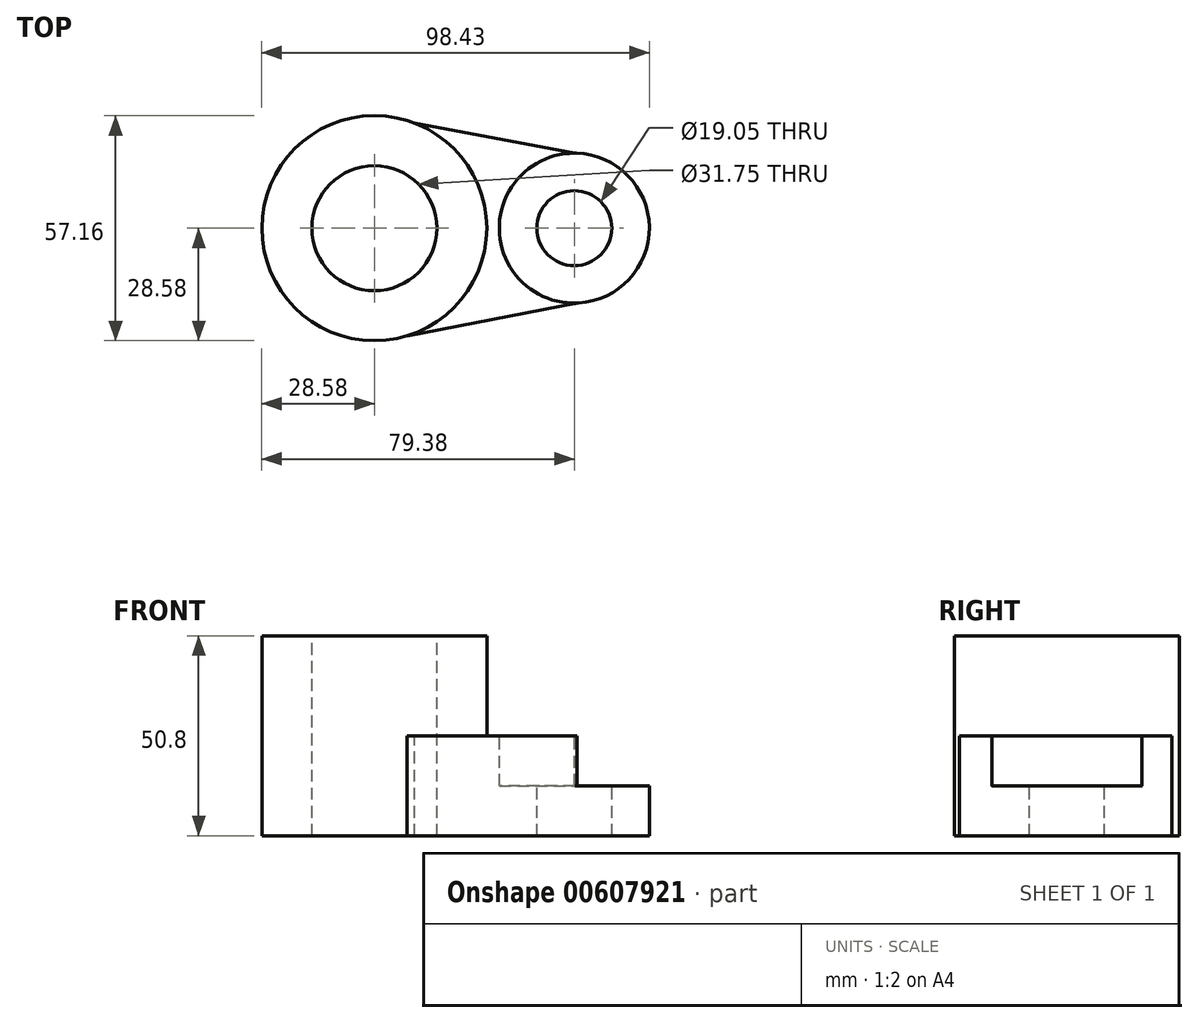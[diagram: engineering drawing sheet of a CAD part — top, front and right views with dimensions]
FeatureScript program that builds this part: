
annotation { "Feature Type Name" : "Feature", "Feature Type Description" : "" }
export const myFeature = defineFeature(function(context is Context, id is Id, definition is map)
    precondition{}
    {
        {
            var Q0;
            Q0=qCreatedBy(makeId("Top.planeOp"),FACE);
            var sketch = newSketch(context, id + "F0", { "sketchPlane" : qUnion([Q0])});
            skCircle(sketch, "E0", {"center": v(0, 0) * mm, "radius": 15.88 * mm});
            skCircle(sketch, "E1", {"center": v(0, 0) * mm, "radius": 28.58 * mm});
            skCircle(sketch, "E2", {"center": v(50.8, 0) * mm, "radius": 19.05 * mm});
            skCircle(sketch, "E3", {"center": v(50.8, 0) * mm, "radius": 9.53 * mm});
            skLineSegment(sketch, "E4", {"start": v(10.28, 26.66) * mm, "end": v(50.88, 19.05) * mm});
            skLineSegment(sketch, "E5", {"start": v(8.3, -27.34) * mm, "end": v(51.47, -19.04) * mm});
            skSolve(sketch);
        }
        {
            var Q0;
            Q0=makeQuery(id+"F0.imprint","IMPRINT",FACE,{"disambiguationData":[TD([[makeQuery(id+"F0.imprint","IMPRINT",EDGE,{"derivedFrom":sQuery(id+"F0.wireOp",EDGE,"E0")}),-1.0]])]});
            var Q1;
            Q1=makeQuery(id+"F0.imprint","IMPRINT",FACE,{"disambiguationData":[TD([[makeQuery(id+"F0.imprint","IMPRINT",EDGE,{"derivedFrom":sQuery(id+"F0.wireOp",EDGE,"E3")}),-1.0]])]});
            var Q2;
            {var subQ0=sQuery(id+"F0.wireOp",EDGE,"E4");Q2=makeQuery(id+"F0.imprint","IMPRINT",FACE,{"disambiguationData":[TD([[makeQuery(id+"F0.imprint","IMPRINT",EDGE,{"derivedFrom":subQ0}),-1.0]])]});}
            extrude(context, id + "F1", {"entities" : qUnion([Q0, Q1, Q2]), "oppositeDirection" : true, "depth" : 25.4 * mm, "offsetDistance" : 25.4 * mm});
        }
        {
            var Q0;
            Q0=makeQuery(id+"F0.imprint","IMPRINT",FACE,{"disambiguationData":[TD([[makeQuery(id+"F0.imprint","IMPRINT",EDGE,{"derivedFrom":sQuery(id+"F0.wireOp",EDGE,"E0")}),-1.0]])]});
            extrude(context, id + "F2", {"entities" : qUnion([Q0]), "operationType" : NewBodyOperationType.ADD, "depth" : 25.4 * mm, "offsetDistance" : 25.4 * mm});
        }
        {
            var Q0;
            Q0=makeQuery(id+"F0.imprint","IMPRINT",FACE,{"disambiguationData":[TD([[makeQuery(id+"F0.imprint","IMPRINT",EDGE,{"derivedFrom":sQuery(id+"F0.wireOp",EDGE,"E3")}),-1.0]])]});
            extrude(context, id + "F3", {"entities" : qUnion([Q0]), "operationType" : NewBodyOperationType.REMOVE, "oppositeDirection" : true, "depth" : 12.7 * mm, "offsetDistance" : 25.4 * mm});
        }
        {
            var Q0;
            {var subQ0=sQuery(id+"F0.wireOp",EDGE,"E5");var subQ1=sQuery(id+"F0.wireOp",EDGE,"E2");Q0=makeQuery(id+"F3.boolean.opBoolean","SPLIT",EDGE,{"disambiguationData":[topologyDisambiguationEdgeConnected([makeQuery(id+"F3.opExtrude","SWEPT_FACE",FACE,{"disambiguationData":[OSD([subQ1])]})])],"derivedFrom":makeQuery(id+"F1.opExtrude","SWEPT_EDGE",EDGE,{"disambiguationData":[OSD([subQ1,subQ0])]})});}
            var Q1;
            {var subQ0=sQuery(id+"F0.wireOp",EDGE,"E4");var subQ1=sQuery(id+"F0.wireOp",EDGE,"E2");Q1=makeQuery(id+"F3.boolean.opBoolean","SPLIT",EDGE,{"disambiguationData":[topologyDisambiguationEdgeConnected([makeQuery(id+"F3.opExtrude","SWEPT_FACE",FACE,{"disambiguationData":[OSD([subQ1])]})])],"derivedFrom":makeQuery(id+"F1.opExtrude","SWEPT_EDGE",EDGE,{"disambiguationData":[OSD([subQ1,subQ0])]})});}
            fillet(context, id + "F4", {"entities" : qUnion([Q0, Q1]), "radius" : 6.35 * mm, "tangentPropagation" : true, "allowEdgeOverflow" : false});
        }
    });
